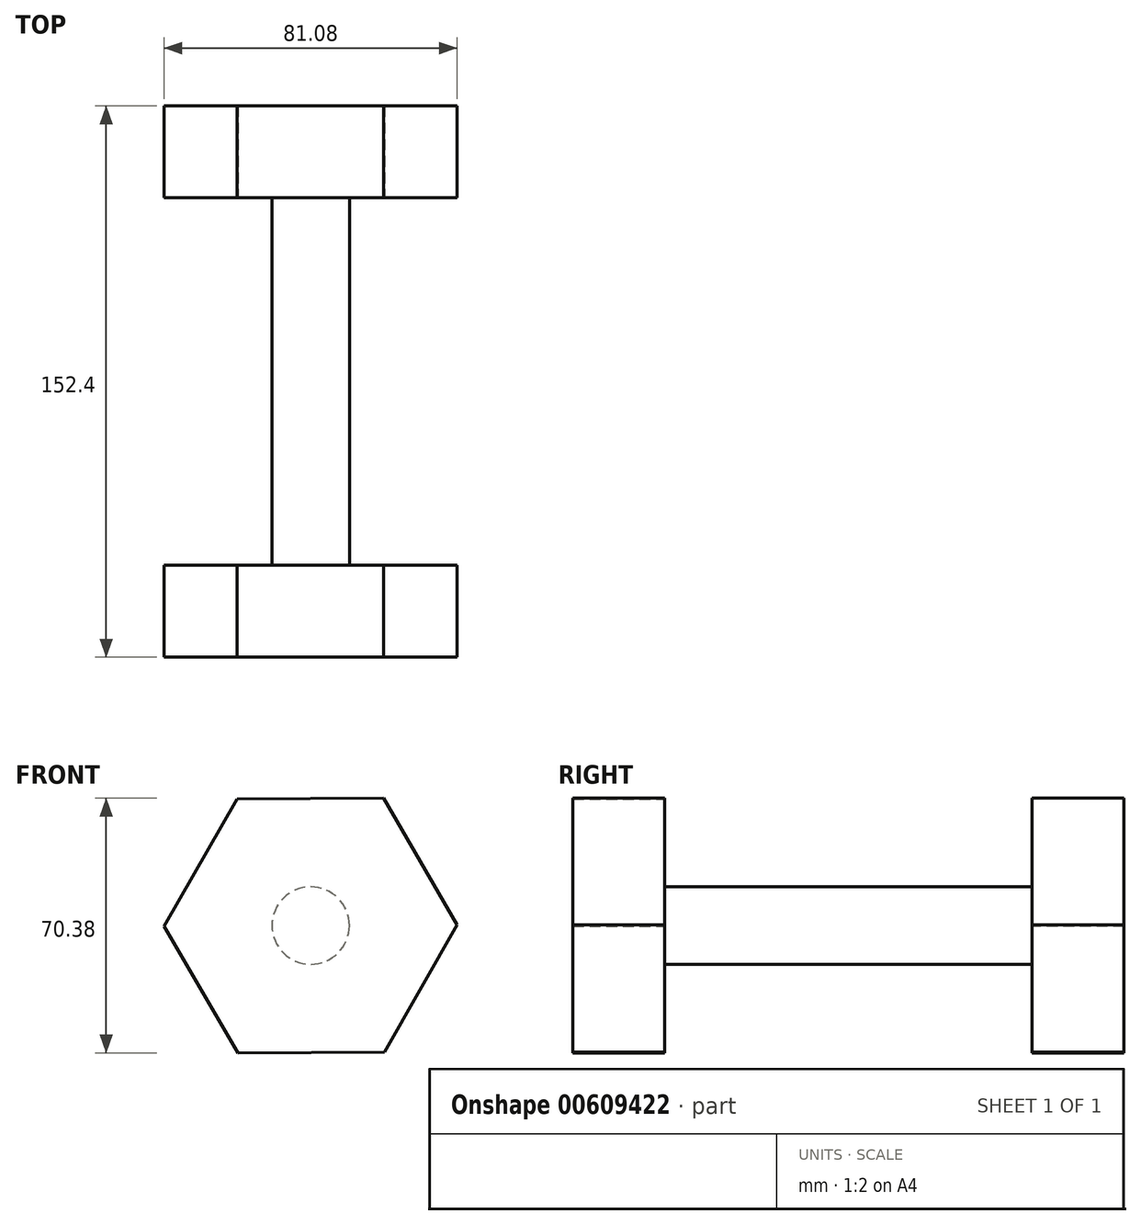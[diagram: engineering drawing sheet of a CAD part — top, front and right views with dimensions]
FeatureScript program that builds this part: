
annotation { "Feature Type Name" : "Feature", "Feature Type Description" : "" }
export const myFeature = defineFeature(function(context is Context, id is Id, definition is map)
    precondition{}
    {
        {
            var Q0;
            Q0=qCreatedBy(makeId("Front.planeOp"),FACE);
            var sketch = newSketch(context, id + "F0", { "sketchPlane" : qUnion([Q0])});
            skCircle(sketch, "E0", {"center": v(0, 0) * mm, "radius": 10.71 * mm});
            skSolve(sketch);
        }
        {
            var Q0;
            Q0 = qSketchRegion(id + "F0", true);
            extrude(context, id + "F1", {"entities" : qUnion([Q0]), "depth" : 50.8 * mm, "offsetDistance" : 25.4 * mm});
        }
        {
            var Q0;
            Q0=makeQuery(id+"F1.opExtrude","CAP_FACE",FACE,{"disambiguationData":[OSD([sQuery(id+"F0.wireOp",EDGE,"E0")])],"isStart":false});
            var sketch = newSketch(context, id + "F2", { "sketchPlane" : qUnion([Q0])});
            skCircle(sketch, "E1.cCircle", {"center": v(0, 0) * mm, "radius": 35.1 * mm, "construction": true});
            skLineSegment(sketch, "E1.0", {"start": v(40.54, 0.15) * mm, "end": v(20.4, -35.03) * mm});
            skLineSegment(sketch, "E1.1", {"start": v(20.4, -35.03) * mm, "end": v(-20.14, -35.19) * mm});
            skLineSegment(sketch, "E1.2", {"start": v(-20.14, -35.19) * mm, "end": v(-40.54, -0.15) * mm});
            skLineSegment(sketch, "E1.3", {"start": v(-40.54, -0.15) * mm, "end": v(-20.4, 35.03) * mm});
            skLineSegment(sketch, "E1.4", {"start": v(-20.4, 35.03) * mm, "end": v(20.14, 35.19) * mm});
            skLineSegment(sketch, "E1.5", {"start": v(20.14, 35.19) * mm, "end": v(40.54, 0.15) * mm});
            skPoint(sketch, "E1.0.midPoint", {"position": v(30.47, -17.44) * mm});
            skSolve(sketch);
        }
        {
            var Q0;
            Q0 = qSketchRegion(id + "F2", true);
            extrude(context, id + "F3", {"entities" : qUnion([Q0]), "operationType" : NewBodyOperationType.ADD, "depth" : 25.4 * mm, "offsetDistance" : 25.4 * mm});
        }
        {
            var Q0;
            Q0=makeQuery(id+"F1.opExtrude","SWEPT_BODY",BODY,{"disambiguationData":[OSD([sQuery(id+"F0.wireOp",EDGE,"E0")])]});
            var Q1;
            Q1=qCreatedBy(makeId("Front.planeOp"),FACE);
            mirror(context, id + "F4", {"operationType" : NewBodyOperationType.ADD, "entities" : qUnion([Q0]), "mirrorPlane" : qUnion([Q1])});
        }
    });
